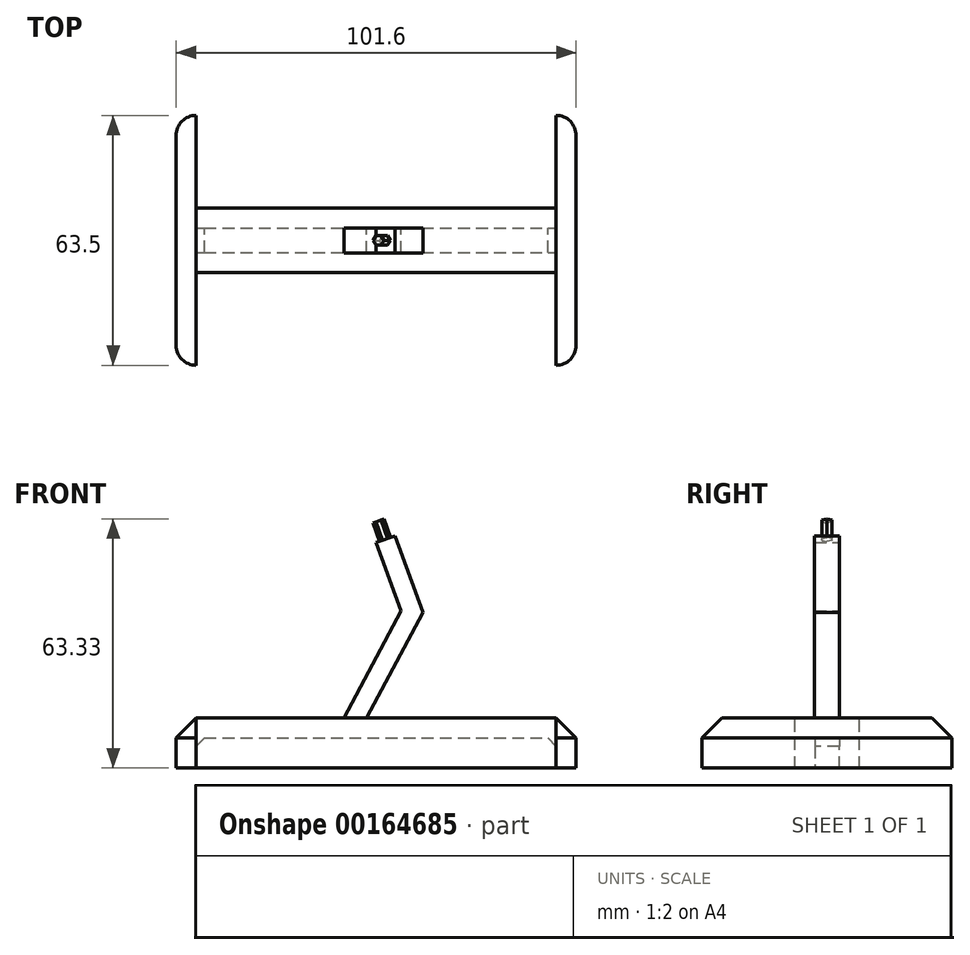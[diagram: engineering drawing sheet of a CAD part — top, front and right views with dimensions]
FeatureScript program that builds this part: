
annotation { "Feature Type Name" : "Feature", "Feature Type Description" : "" }
export const myFeature = defineFeature(function(context is Context, id is Id, definition is map)
    precondition{}
    {
        {
            var Q0;
            Q0=qCreatedBy(makeId("Front.planeOp"),FACE);
            var sketch = newSketch(context, id + "F0", { "sketchPlane" : qUnion([Q0])});
            skLineSegment(sketch, "E0.bottom", {"start": v(50.8, 6.35) * mm, "end": v(-50.8, 6.35) * mm});
            skLineSegment(sketch, "E0.top", {"start": v(50.8, -6.35) * mm, "end": v(-50.8, -6.35) * mm});
            skLineSegment(sketch, "E0.left", {"start": v(50.8, 6.35) * mm, "end": v(50.8, -6.35) * mm});
            skLineSegment(sketch, "E0.right", {"start": v(-50.8, 6.35) * mm, "end": v(-50.8, -6.35) * mm});
            skPoint(sketch, "E0.middle", {"position": v(0, 0) * mm});
            skLineSegment(sketch, "E1", {"start": v(-8.2, 6.35) * mm, "end": v(6.35, 33.56) * mm});
            skLineSegment(sketch, "E2", {"start": v(6.35, 33.56) * mm, "end": v(0, 50.93) * mm});
            skLineSegment(sketch, "E3.0", {"start": v(11.9, 33.17) * mm, "end": v(4.77, 52.68) * mm});
            skLineSegment(sketch, "E3.1", {"start": v(-2.44, 6.35) * mm, "end": v(11.9, 33.17) * mm});
            skLineSegment(sketch, "E4", {"start": v(0, 50.93) * mm, "end": v(4.77, 52.68) * mm});
            skPoint(sketch, "E5", {"position": v(0, 6.35) * mm});
            skSolve(sketch);
        }
        {
            var Q0;
            Q0=makeQuery(id+"F0.imprint","IMPRINT",FACE,{"disambiguationData":[TD([[makeQuery(id+"F0.imprint","IMPRINT",EDGE,{"derivedFrom":sQuery(id+"F0.wireOp",EDGE,"E0.top")}),-1.0]])]});
            extrude(context, id + "F1", {"entities" : qUnion([Q0]), "endBound" : BoundingType.SYMMETRIC, "depth" : 63.5 * mm});
        }
        {
            var Q0;
            {var subQ0=sQuery(id+"F0.wireOp",EDGE,"E1");Q0=makeQuery(id+"F0.imprint","IMPRINT",FACE,{"disambiguationData":[TD([[makeQuery(id+"F0.imprint","IMPRINT",EDGE,{"derivedFrom":subQ0}),-1.0]])]});}
            extrude(context, id + "F2", {"entities" : qUnion([Q0]), "operationType" : NewBodyOperationType.ADD, "endBound" : BoundingType.SYMMETRIC, "depth" : 6.35 * mm});
        }
        {
            var Q0;
            Q0=makeQuery(id+"F1.opExtrude","CAP_EDGE",EDGE,{"disambiguationData":[OSD([sQuery(id+"F0.wireOp",EDGE,"E0.right")])],"isStart":false});
            var Q1;
            Q1=makeQuery(id+"F1.opExtrude","CAP_EDGE",EDGE,{"disambiguationData":[OSD([sQuery(id+"F0.wireOp",EDGE,"E0.left")])],"isStart":false});
            var Q2;
            Q2=makeQuery(id+"F1.opExtrude","CAP_EDGE",EDGE,{"disambiguationData":[OSD([sQuery(id+"F0.wireOp",EDGE,"E0.left")])],"isStart":true});
            var Q3;
            Q3=makeQuery(id+"F1.opExtrude","CAP_EDGE",EDGE,{"disambiguationData":[OSD([sQuery(id+"F0.wireOp",EDGE,"E0.right")])],"isStart":true});
            fillet(context, id + "F3", {"entities" : qUnion([Q0, Q1, Q2, Q3]), "radius" : 5.08 * mm, "tangentPropagation" : true, "allowEdgeOverflow" : false});
        }
        {
            var Q0;
            Q0=makeQuery(id+"F1.opExtrude","SWEPT_EDGE",EDGE,{"disambiguationData":[OSD([sQuery(id+"F0.wireOp",EDGE,"E0.bottom"),sQuery(id+"F0.wireOp",EDGE,"E0.left")])]});
            chamfer(context, id + "F4", {"entities" : qUnion([Q0]), "width" : 5.08 * mm, "tangentPropagation" : true});
        }
        {
            var Q0;
            Q0=makeQuery(id+"F2.opExtrude","SWEPT_FACE",FACE,{"disambiguationData":[OSD([sQuery(id+"F0.wireOp",EDGE,"E4")])]});
            var sketch = newSketch(context, id + "F5", { "sketchPlane" : qUnion([Q0])});
            skLineSegment(sketch, "E6", {"start": v(19.25, 1.25) * mm, "end": v(20.6, 1.25) * mm});
            skLineSegment(sketch, "E7", {"start": v(20.6, 1.25) * mm, "end": v(21.42, 0) * mm});
            skLineSegment(sketch, "E8", {"start": v(19.25, 1.25) * mm, "end": v(18.42, 0) * mm});
            skLineSegment(sketch, "E9.MirrorCS", {"start": v(20.6, -1.25) * mm, "end": v(21.42, 0) * mm});
            skLineSegment(sketch, "E10.MirrorCS", {"start": v(19.25, -1.25) * mm, "end": v(18.42, 0) * mm});
            skPoint(sketch, "E11", {"position": v(22.57, 0) * mm});
            skPoint(sketch, "E12", {"position": v(17.5, 0) * mm});
            skLineSegment(sketch, "E13", {"start": v(19.25, -1.25) * mm, "end": v(20.6, -1.25) * mm});
            skSolve(sketch);
        }
        {
            var Q0;
            Q0 = qSketchRegion(id + "F5", true);
            extrude(context, id + "F6", {"entities" : qUnion([Q0]), "operationType" : NewBodyOperationType.ADD, "depth" : 5 * mm});
        }
        {
            var Q0;
            Q0=makeQuery(id+"F1.opExtrude","SWEPT_FACE",FACE,{"disambiguationData":[OSD([sQuery(id+"F0.wireOp",EDGE,"E0.bottom")])]});
            var sketch = newSketch(context, id + "F7", { "sketchPlane" : qUnion([Q0])});
            skLineSegment(sketch, "E14.bottom", {"start": v(-45.72, -8.18) * mm, "end": v(45.72, -8.18) * mm});
            skLineSegment(sketch, "E14.top", {"start": v(-45.72, -31.96) * mm, "end": v(45.72, -31.96) * mm});
            skLineSegment(sketch, "E14.left", {"start": v(-45.72, -8.18) * mm, "end": v(-45.72, -31.96) * mm});
            skLineSegment(sketch, "E14.right", {"start": v(45.72, -8.17) * mm, "end": v(45.72, -31.96) * mm});
            skLineSegment(sketch, "E15.MirrorCS", {"start": v(-45.72, 8.18) * mm, "end": v(45.72, 8.18) * mm});
            skLineSegment(sketch, "E16.MirrorCS", {"start": v(-45.72, 8.18) * mm, "end": v(-45.72, 31.96) * mm});
            skLineSegment(sketch, "E17.MirrorCS", {"start": v(-45.72, 31.96) * mm, "end": v(45.72, 31.96) * mm});
            skLineSegment(sketch, "E18.MirrorCS", {"start": v(45.72, 8.17) * mm, "end": v(45.72, 31.96) * mm});
            skSolve(sketch);
        }
        {
            var Q0;
            {var subQ0=sQuery(id+"F7.wireOp",EDGE,"E14.bottom");Q0=makeQuery(id+"F7.imprint","IMPRINT",FACE,{"disambiguationData":[TD([[makeQuery(id+"F7.imprint","IMPRINT",EDGE,{"derivedFrom":subQ0}),-1.0]])]});}
            var Q1;
            {var subQ0=sQuery(id+"F7.wireOp",EDGE,"E15.MirrorCS");Q1=makeQuery(id+"F7.imprint","IMPRINT",FACE,{"disambiguationData":[TD([[makeQuery(id+"F7.imprint","IMPRINT",EDGE,{"derivedFrom":subQ0}),1.0]])]});}
            var Q2;
            {var subQ0=sQuery(id+"F7.wireOp",EDGE,"E14.top");Q2=makeQuery(id+"F7.imprint","IMPRINT",FACE,{"disambiguationData":[TD([[makeQuery(id+"F7.imprint","IMPRINT",EDGE,{"derivedFrom":subQ0}),1.0]])]});}
            var Q3;
            {var subQ3=sQuery(id+"F7.wireOp",EDGE,"E17.MirrorCS");Q3=makeQuery(id+"F7.imprint","IMPRINT",FACE,{"disambiguationData":[TD([[makeQuery(id+"F7.imprint","IMPRINT",EDGE,{"derivedFrom":subQ3}),-1.0]])]});}
            extrude(context, id + "F8", {"entities" : qUnion([Q0, Q1, Q2, Q3]), "operationType" : NewBodyOperationType.REMOVE, "endBound" : BoundingType.THROUGH_ALL, "oppositeDirection" : true, "depth" : 25.4 * mm});
        }
        {
            var Q0;
            Q0=makeQuery(id+"F1.opExtrude","SWEPT_FACE",FACE,{"disambiguationData":[OSD([sQuery(id+"F0.wireOp",EDGE,"E0.top")])]});
            shell(context, id + "F9", {"entities" : qUnion([Q0]), "thickness" : 5.08 * mm});
        }
    });
